# Revit family: 75029
name_source: partatom
category: Doors
revit_build: Autodesk Revit 2018 (Build: 20170223_1515(x64)
units: mm (PartAtom-declared; Revit-internal decimal feet)

## family parameters
Always vertical = Yes
Cut with Voids When Loaded = No
Host = Wall
OmniClass Number = 23.30.10.17.17
OmniClass Title = Folding Doors and Grilles
Room Calculation Point = No
Shared = No

## types (1)
- Standard
    04 CSI = 08 41 13
    95 CSI = 8411
    Assembly Code = C1010.2010
    Cost Info = http://www.nanawall.com
    Description = NanaGlass All Glass Opening Window Wall
    Disclaimer = Please note that the Revit model is for schematic purposes only.  To obtain a detailed 3D model, please go to the NanaWall's configurator at www.nanawall.com.
    Engineering Details URL = http://www.nanawall.com
    Exterior Wall Offset = 4"
    Filler = <By Category>
    Function = Interior
    Glass Material = Glass - NanaWall - Generic
    Glazing Options = http://www.nanawall.com
    Height = 9' - 6"
    Height Constraint = 9' - 2"
    Installation and Service URL = http://www.nanawall.com
    Manufacturer = NanaWall Systems, Inc.
    Manufacturer Fax = (415) 383-0312
    Max Panel Height = 9' - 2"
    Model = SL 25
    NanaWall Configurator = http://www.nanawall.com
    Opening Width = 9' - 10 7/64"
    Panel Height = 9' - 2"
    Performance URL = http://www.nanawall.com
    Product Page URL = http://www.nanawall.com
    Rough Height = 9' - 2"
    Rough Width = 9' - 10 7/64"
    Sash = Metal - NanaWall - Aluminum
    Sills Available = Raised, Low Profile Saddle, Flush
    Subcategory = Folding Door
    Thickness = 1 1/4"
    URL = http://www.nanawall.com
    Wall Closure = By host
    Warranty URL = http://www.nanawall.com
    Width = 10' - 0"

## geometry (parser evidence)
native form markers: Blend x2, Sweep x15
no freeform markers — native parametric forms only
